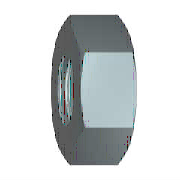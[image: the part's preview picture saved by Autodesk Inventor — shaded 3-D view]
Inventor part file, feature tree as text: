
AUTODESK INVENTOR PART (.ipt)
format: ipt  version: 2023 (Build 270158000, 158)  size: 174,080 bytes
history: native  units: mm (DEFAULTED — no unit token found)
features: sketch x3, other x2, extrude x1, hole x1, plane x1
ambient origin geometry x7: Origin, YZ Plane, XZ Plane, X Axis, Y Axis, Z Axis, Center Point
bodies: Solid1 (feature_tree)
feature tree (8):
  extrude  "Corpo"  Depth=27.712813mm
  other  "Smusso1"
  hole  "Filettatura"  [1 undecoded]
  other  "Work Axis1"
  plane  "Work Plane1"
  sketch  "Schizzo1"
  sketch  "Schizzo2"
  sketch  "Schizzo3"
note: 1 required parameter value undecoded (feature->parameter linkage not recoverable at this tier; creation-order binding heuristic only, values carry confidence <= 0.55)
